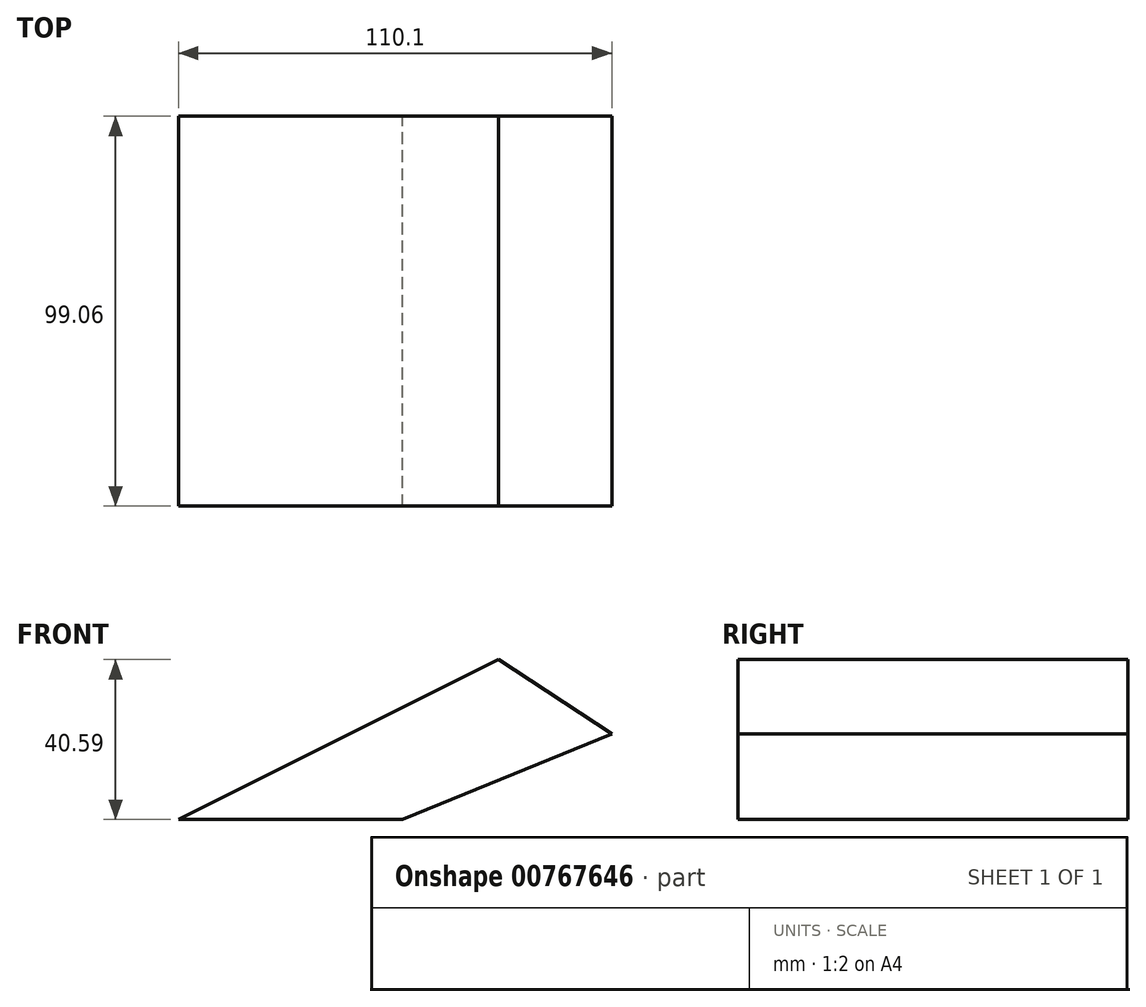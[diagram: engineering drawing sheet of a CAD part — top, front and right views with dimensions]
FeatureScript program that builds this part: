
annotation { "Feature Type Name" : "Feature", "Feature Type Description" : "" }
export const myFeature = defineFeature(function(context is Context, id is Id, definition is map)
    precondition{}
    {
        {
            var Q0;
            Q0=qCreatedBy(makeId("Front.planeOp"),FACE);
            var sketch = newSketch(context, id + "F0", { "sketchPlane" : qUnion([Q0])});
            skLineSegment(sketch, "E0", {"start": v(0, 0) * mm, "end": v(-56.95, 0) * mm});
            skLineSegment(sketch, "E1", {"start": v(-56.95, 0) * mm, "end": v(24.3, 40.59) * mm});
            skLineSegment(sketch, "E2", {"start": v(24.3, 40.59) * mm, "end": v(53.15, 21.75) * mm});
            skLineSegment(sketch, "E3", {"start": v(53.15, 21.75) * mm, "end": v(0, 0) * mm});
            skSolve(sketch);
        }
        {
            var Q0;
            Q0=makeQuery(id+"F0.imprint","IMPRINT",FACE,{"disambiguationData":[TD([[makeQuery(id+"F0.imprint","IMPRINT",EDGE,{"derivedFrom":sQuery(id+"F0.wireOp",EDGE,"E0")}),-1.0]])]});
            extrude(context, id + "F1", {"entities" : qUnion([Q0]), "depth" : 99.06 * mm, "offsetDistance" : 25.4 * mm});
        }
    });
